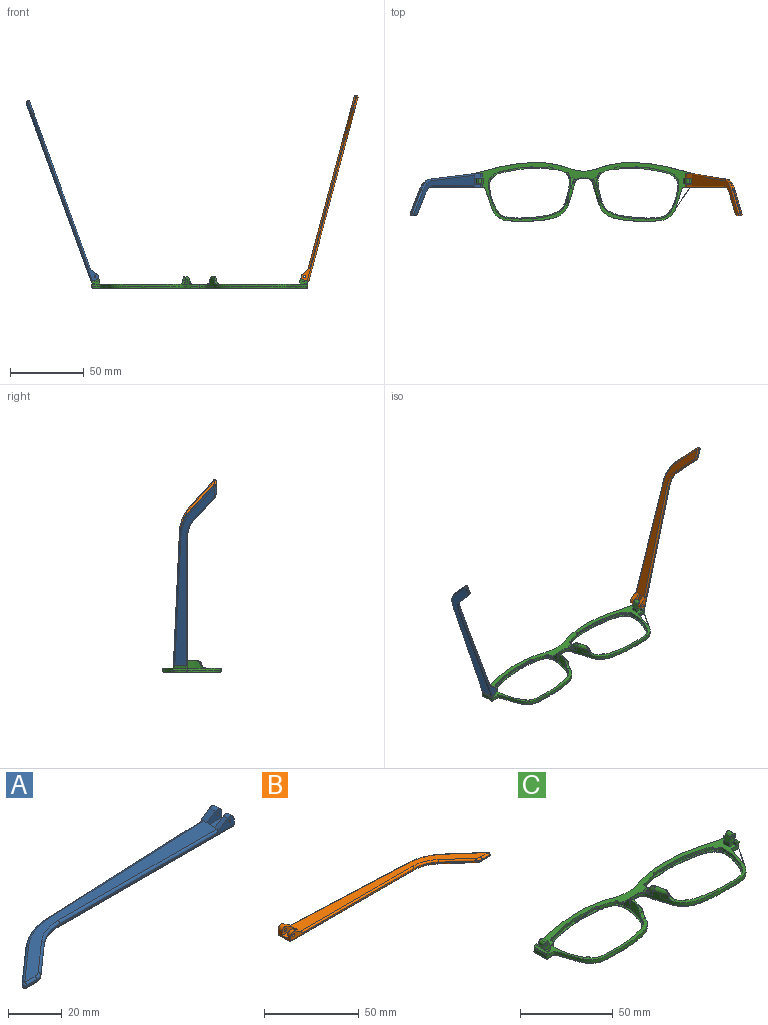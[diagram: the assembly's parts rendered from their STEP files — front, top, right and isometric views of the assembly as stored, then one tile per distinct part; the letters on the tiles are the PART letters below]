
ASSEMBLY  parts=3 mates=2
PART A: 43 faces, bbox 130.2x29.5x5.9 mm
  f0: plane 9.62x3.72mm, normal (1,0,0), area 24.7mm2, adj f1,f3,f4,f5,f10,f16,f18,f28
  f1: cylinder r=2.2mm len=3.45mm, axis (0,-1,0), area 11mm2, adj f0,f2,f4,f37
  f2: plane 6.01x3.91mm, normal (-0.55,0,0.84), area 12.7mm2, adj f1,f4,f9,f19,f37
  f3: plane 2.26x0.1mm, normal (0,0,1), area 0.1mm2, adj f0,f5,f18
  f4: plane 92.1x4.9mm, normal (0,-1,0), area 79.9mm2, adj f0,f1,f2,f14,f19,f36,f42
  f5: plane 93.42x4.13mm, normal (-0.04,1,0), area 64.8mm2, adj f0,f3,f11,f15,f17,f27,f28
  f6: plane 17.82x15.72mm, normal (-0.66,0.75,0), area 14.3mm2, adj f11,f12,f25,f30
  f7: plane 5.46x0.6mm, normal (0,-1,0), area 3.3mm2, adj f12,f13,f23,f32
  f8: plane 14.99x13.23mm, normal (0.66,-0.75,0), area 12mm2, adj f13,f14,f21,f34
  f9: plane 121.18x26.73mm, normal (0,0,1), area 627.7mm2, adj f2,f17,f19,f20,f21,f22,f23,f25
  f10: plane 129.1x27.08mm, normal (0,0,-1), area 686.5mm2, adj f0,f28,f29,f30,f32,f33,f34,f35
  f11: cylinder r=30mm len=18.52mm, axis (0,0,-1), area 12.2mm2, adj f5,f6,f26,f29
  f12: cylinder r=1mm len=1.75mm, axis (0,0,-1), area 1.5mm2, adj f6,f7,f24,f31
  f13: cylinder r=5mm len=3.31mm, axis (0,0,-1), area 2.2mm2, adj f7,f8,f22,f33
  f14: cylinder r=20mm len=13.23mm, axis (0,0,1), area 8.7mm2, adj f4,f8,f20,f35
  f15: plane 5.66x0.25mm, normal (0,0,-1), area 0.7mm2, adj f5,f17,f18
  f16: cylinder r=2.2mm len=3.45mm, axis (0,-1,0), area 14.8mm2, adj f0,f17,f18,f38
  f17: plane 6.01x3.91mm, normal (-0.55,0,0.84), area 16.9mm2, adj f5,f9,f15,f16,f18,f27,f38
  f18: plane 7.92x3.3mm, normal (0,1,0), area 15.9mm2, adj f0,f3,f15,f16,f17,f41
  f19: cylinder r=1mm len=84.18mm, axis (-1,0,0), area 131.4mm2, adj f2,f4,f9,f20
  f20: torus R=21mm, axis (0,0,1), area 23.1mm2, adj f9,f14,f19,f21
  f21: cylinder r=1mm len=15.65mm, axis (-0.75,-0.66,0), area 31.4mm2, adj f8,f9,f20,f22
  f22: torus R=4mm, axis (0,0,1), area 5.3mm2, adj f9,f13,f21,f23
  f23: cylinder r=1mm len=5.46mm, axis (-1,0,0), area 8.6mm2, adj f7,f9,f22,f24
  f24: sphere r=1mm, area 2.4mm2, adj f12,f23,f25
  f25: cylinder r=1mm len=18.48mm, axis (0.75,0.66,0), area 37.3mm2, adj f6,f9,f24,f26
  f26: torus R=29mm, axis (0,0,1), area 31.6mm2, adj f9,f11,f25,f27
  f27: cylinder r=1mm len=85.5mm, axis (1,0.04,0), area 133.5mm2, adj f5,f9,f17,f26
  f28: cylinder r=1mm len=93.46mm, axis (-1,-0.04,0), area 146.9mm2, adj f0,f5,f10,f29
  f29: torus R=29mm, axis (0,0,1), area 31.6mm2, adj f10,f11,f28,f30
  f30: cylinder r=1mm len=18.48mm, axis (-0.75,-0.66,0), area 37.3mm2, adj f6,f10,f29,f31
  f31: sphere r=1mm, area 2.4mm2, adj f12,f30,f32
  f32: cylinder r=1mm len=5.46mm, axis (1,0,0), area 8.6mm2, adj f7,f10,f31,f33
  f33: torus R=4mm, axis (0,0,1), area 5.3mm2, adj f10,f13,f32,f34
  f34: cylinder r=1mm len=15.65mm, axis (0.75,0.66,0), area 31.4mm2, adj f8,f10,f33,f35
  f35: torus R=21mm, axis (0,0,1), area 23.1mm2, adj f10,f14,f34,f36
  f36: cylinder r=1mm len=92.1mm, axis (1,0,0), area 144.7mm2, adj f0,f4,f10,f35
  f37: plane 7.92x4.7mm, normal (0,1,0), area 27mm2, adj f0,f1,f2,f39,f40,f42
  f38: plane 7.92x4.7mm, normal (0,-1,0), area 27mm2, adj f0,f16,f17,f39,f40,f41
  f39: plane 7.92x4.1mm, normal (0,0,1), area 32.5mm2, adj f0,f37,f38,f40
  f40: plane 4.1x1.4mm, normal (1,0,0), area 5.7mm2, adj f9,f37,f38,f39
  f41: cylinder r=0.5mm len=3.1mm, axis (0,-1,0), area 9.7mm2, adj f18,f38
  f42: cylinder r=0.5mm len=2.3mm, axis (0,-1,0), area 7.2mm2, adj f4,f37
PART B: 43 faces, bbox 130.2x29.5x5.9 mm
  f0: plane 9.62x3.72mm, normal (-1,0,0), area 24.7mm2, adj f1,f3,f4,f5,f10,f16,f18,f28
  f1: cylinder r=2.2mm len=3.45mm, axis (0,-1,0), area 11mm2, adj f0,f2,f4,f37
  f2: plane 6.01x3.91mm, normal (0.55,0,0.84), area 12.7mm2, adj f1,f4,f9,f19,f37
  f3: plane 2.26x0.1mm, normal (0,0,1), area 0.1mm2, adj f0,f5,f18
  f4: plane 92.1x4.9mm, normal (0,-1,0), area 78.2mm2, adj f0,f1,f2,f14,f19,f36,f42
  f5: plane 93.42x4.13mm, normal (0.04,1,0), area 64.8mm2, adj f0,f3,f11,f15,f17,f27,f28
  f6: plane 17.82x15.72mm, normal (0.66,0.75,0), area 14.3mm2, adj f11,f12,f25,f30
  f7: plane 5.46x0.6mm, normal (0,-1,0), area 3.3mm2, adj f12,f13,f23,f32
  f8: plane 14.99x13.23mm, normal (-0.66,-0.75,0), area 12mm2, adj f13,f14,f21,f34
  f9: plane 121.18x26.73mm, normal (0,0,1), area 627.7mm2, adj f2,f17,f19,f20,f21,f22,f23,f25
  f10: plane 129.1x27.08mm, normal (0,0,-1), area 686.5mm2, adj f0,f28,f29,f30,f32,f33,f34,f35
  f11: cylinder r=30mm len=18.52mm, axis (0,0,-1), area 12.2mm2, adj f5,f6,f26,f29
  f12: cylinder r=1mm len=1.75mm, axis (0,0,-1), area 1.5mm2, adj f6,f7,f24,f31
  f13: cylinder r=5mm len=3.31mm, axis (0,0,-1), area 2.2mm2, adj f7,f8,f22,f33
  f14: cylinder r=20mm len=13.23mm, axis (0,0,1), area 8.7mm2, adj f4,f8,f20,f35
  f15: plane 5.66x0.25mm, normal (0,0,-1), area 0.7mm2, adj f5,f17,f18
  f16: cylinder r=2.2mm len=3.45mm, axis (0,-1,0), area 14.8mm2, adj f0,f17,f18,f38
  f17: plane 6.01x3.91mm, normal (0.55,0,0.84), area 16.9mm2, adj f5,f9,f15,f16,f18,f27,f38
  f18: plane 7.92x3.3mm, normal (0,1,0), area 14.3mm2, adj f0,f3,f15,f16,f17,f41
  f19: cylinder r=1mm len=84.18mm, axis (1,0,0), area 131.4mm2, adj f2,f4,f9,f20
  f20: torus R=21mm, axis (0,0,1), area 23.1mm2, adj f9,f14,f19,f21
  f21: cylinder r=1mm len=15.65mm, axis (0.75,-0.66,0), area 31.4mm2, adj f8,f9,f20,f22
  f22: torus R=4mm, axis (0,0,1), area 5.3mm2, adj f9,f13,f21,f23
  f23: cylinder r=1mm len=5.46mm, axis (1,0,0), area 8.6mm2, adj f7,f9,f22,f24
  f24: sphere r=1mm, area 2.4mm2, adj f12,f23,f25
  f25: cylinder r=1mm len=18.48mm, axis (-0.75,0.66,0), area 37.3mm2, adj f6,f9,f24,f26
  f26: torus R=29mm, axis (0,0,1), area 31.6mm2, adj f9,f11,f25,f27
  f27: cylinder r=1mm len=85.5mm, axis (-1,0.04,0), area 133.5mm2, adj f5,f9,f17,f26
  f28: cylinder r=1mm len=93.46mm, axis (1,-0.04,0), area 146.9mm2, adj f0,f5,f10,f29
  f29: torus R=29mm, axis (0,0,1), area 31.6mm2, adj f10,f11,f28,f30
  f30: cylinder r=1mm len=18.48mm, axis (0.75,-0.66,0), area 37.3mm2, adj f6,f10,f29,f31
  f31: sphere r=1mm, area 2.4mm2, adj f12,f30,f32
  f32: cylinder r=1mm len=5.46mm, axis (-1,0,0), area 8.6mm2, adj f7,f10,f31,f33
  f33: torus R=4mm, axis (0,0,1), area 5.3mm2, adj f10,f13,f32,f34
  f34: cylinder r=1mm len=15.65mm, axis (-0.75,0.66,0), area 31.4mm2, adj f8,f10,f33,f35
  f35: torus R=21mm, axis (0,0,1), area 23.1mm2, adj f10,f14,f34,f36
  f36: cylinder r=1mm len=92.1mm, axis (-1,0,0), area 144.7mm2, adj f0,f4,f10,f35
  f37: plane 7.92x4.7mm, normal (0,1,0), area 25.4mm2, adj f0,f1,f2,f39,f40,f42
  f38: plane 7.92x4.7mm, normal (0,-1,0), area 25.4mm2, adj f0,f16,f17,f39,f40,f41
  f39: plane 7.92x4.1mm, normal (0,0,1), area 32.5mm2, adj f0,f37,f38,f40
  f40: plane 4.1x1.4mm, normal (-1,0,0), area 5.7mm2, adj f9,f37,f38,f39
  f41: cylinder r=0.88mm len=3.1mm, axis (0,-1,0), area 17mm2, adj f18,f38
  f42: cylinder r=0.88mm len=2.3mm, axis (0,-1,0), area 12.6mm2, adj f4,f37
PART C: 120 faces, bbox 148.1x40.9x10.4 mm
  f0: bspline ~1.82x1.22mm, area 0.7mm2, adj f1,f116,f118,f119
  f1: bspline ~2.66x2.04mm, area 1.9mm2, adj f0,f2,f115,f116,f119
  f2: bspline ~3.55x3.47mm, area 3.7mm2, adj f1,f3,f114,f115,f119
  f3: plane 147.7x40.47mm, normal (0,0,1), area 882.9mm2, adj f2,f4,f16,f17,f18,f19,f20,f21
  f4: plane 1.23x0.04mm, normal (0,0,1), area 0mm2, adj f3,f5,f116
  f5: plane 2.76x2.53mm, normal (0,-1,0), area 3.9mm2, adj f4,f6,f15,f16,f24
  f6: plane 9.65x1.24mm, normal (0,0,1), area 8.2mm2, adj f5,f7,f14,f15,f19,f20,f21,f24
  f7: plane 5.77x5.06mm, normal (0,-1,0), area 17mm2, adj f6,f8,f9,f11,f12,f13,f14,f23
  f8: cylinder r=1.98mm len=4mm, axis (0,-1,0), area 12.4mm2, adj f7,f12,f14,f21
  f9: plane 4x3.31mm, normal (-0.94,0,0.34), area 14.1mm2, adj f7,f10,f11,f21
  f10: plane 4x0.02mm, normal (0.34,0,0.94), area 0.1mm2, adj f9,f21,f22
  f11: cylinder r=1.98mm len=4mm, axis (0,1,0), area 12.4mm2, adj f7,f9,f12,f21
  f12: plane 4x0.01mm, normal (0.34,0,0.94), area 0mm2, adj f7,f8,f11,f21
  f13: cylinder r=0.88mm len=4mm, axis (0,-1,0), area 22mm2, adj f7,f21
  f14: plane 4x2.21mm, normal (0.94,0,-0.34), area 9.4mm2, adj f6,f7,f8,f21
  f15: plane 9.71x1.44mm, normal (0.34,0,0.94), area 13.9mm2, adj f5,f6,f16,f17,f18,f19
  f16: cone r=1mm half-angle=20deg, axis (0,0,1), area 2.3mm2, adj f3,f5,f15,f17
  f17: plane 7.67x1.6mm, normal (0.94,0,-0.34), area 13mm2, adj f3,f15,f16,f18
  f18: cylinder r=1mm len=2.28mm, axis (-0.34,0,-0.94), area 3mm2, adj f3,f15,f17,f19
  f19: plane 2.1x1.69mm, normal (0,1,0), area 2.8mm2, adj f3,f6,f15,f18,f20
  f20: plane 3.3x2.1mm, normal (-1,0,0), area 6.9mm2, adj f3,f6,f19,f21
  f21: plane 6.97x5.07mm, normal (0,1,0), area 22.7mm2, adj f3,f6,f8,f9,f10,f11,f12,f13
  f22: plane 4x2.36mm, normal (-1,0,0), area 9.5mm2, adj f3,f10,f21,f23
  f23: plane 3.2x2.36mm, normal (0,-1,0), area 5.7mm2, adj f3,f7,f22,f24
  f24: plane 2.35x2.1mm, normal (-1,0,0), area 4.9mm2, adj f3,f5,f6,f7,f23
  f25: bspline ~3.69x3.66mm, area 7.8mm2, adj f3,f26,f31,f59,f116
  f26: bspline ~7.26x7.26mm, area 6.3mm2, adj f25,f27,f31,f59
  f27: bspline ~10.3x4.84mm, area 21.4mm2, adj f26,f28,f31,f59,f116,f119
  f28: plane 3.63x0.97mm, normal (0,0,1), area 0.3mm2, adj f27,f29,f59
  f29: bspline ~8.14x4.16mm, area 6.6mm2, adj f28,f30,f59,f114,f119
  f30: extruded ~4.98x1.44mm, area 6.9mm2, adj f29,f59
  f31: extruded ~4.44x3.32mm, area 15.1mm2, adj f25,f26,f27,f32,f116
  f32: plane 4.46x1.45mm, normal (0,0,1), area 0.1mm2, adj f31,f116
  f33: cylinder r=1.3mm len=1.78mm, axis (0,0,1), area 1.3mm2, adj f3,f34,f59
  f34: plane 1.79x1.31mm, normal (0,0,-1), area 0.9mm2, adj f33,f59
  f35: cylinder r=1.3mm len=1.93mm, axis (0,0,1), area 1.5mm2, adj f3,f36,f59
  f36: plane 1.95x1.68mm, normal (0,0,-1), area 1.5mm2, adj f35,f59
  f37: cylinder r=2.28mm len=3.13mm, axis (0,0,1), area 2.5mm2, adj f3,f38,f59
  f38: plane 3.14x2.79mm, normal (0,0,-1), area 3.9mm2, adj f37,f59
  f39: extruded ~8.63x2.7mm, area 18.4mm2, adj f3,f40,f58,f59
  f40: bspline ~56.23x35.9mm, area 235.3mm2, adj f39,f41,f42
  f41: plane 56.09x35.62mm, normal (0,0,1), area 124.3mm2, adj f40,f58
  f42: plane 144.78x37.85mm, normal (0,0,-1), area 582.4mm2, adj f40,f43,f46,f49,f50,f51,f52,f54
  f43: bspline ~56.22x35.9mm, area 235.3mm2, adj f42,f44,f81
  f44: plane 56.09x35.62mm, normal (0,0,1), area 124.3mm2, adj f43,f45
  f45: extruded ~55.59x35.37mm, area 140.2mm2, adj f44,f81,f88
  f46: bspline ~8.99x1.23mm, area 12.6mm2, adj f42,f47,f48,f116
  f47: bspline ~1x1mm, area 0.8mm2, adj f46,f57,f116
  f48: bspline ~1.04x1mm, area 0.7mm2, adj f46,f49,f116
  f49: bspline ~45.86x8.59mm, area 59.8mm2, adj f42,f48,f50,f116
  f50: bspline ~37.01x6.7mm, area 56.6mm2, adj f42,f49,f51,f113
  f51: bspline ~37.01x6.7mm, area 56.6mm2, adj f42,f50,f52,f112
  f52: bspline ~45.86x8.59mm, area 59.8mm2, adj f42,f51,f53,f111
  f53: bspline ~1.04x1mm, area 0.8mm2, adj f52,f54,f111
  f54: bspline ~8.99x1.23mm, area 12.6mm2, adj f42,f53,f55,f111
  f55: bspline ~1x1mm, area 0.8mm2, adj f54,f56,f111
  f56: bspline ~73.83x30.39mm, area 161.7mm2, adj f42,f55,f57,f111
  f57: bspline ~73.27x30.39mm, area 161.7mm2, adj f42,f47,f56,f116
  f58: extruded ~55.59x35.37mm, area 140.2mm2, adj f39,f41,f59
  f59: extruded ~55.59x35.37mm, area 208.7mm2, adj f3,f25,f26,f27,f28,f29,f30,f33
  f60: plane 3.25x1.39mm, normal (0,0,-1), area 2.1mm2, adj f59,f61
  f61: cylinder r=2.28mm len=3.21mm, axis (0,0,1), area 2.2mm2, adj f3,f59,f60,f114
  f62: bspline ~6.38x2.14mm, area 2.6mm2, adj f3,f63,f115,f116
  f63: bspline ~6.38x2.14mm, area 2.6mm2, adj f3,f62,f64,f111
  f64: bspline ~2.1x1.46mm, area 0.6mm2, adj f63,f65,f77,f111
  f65: bspline ~2.66x2.03mm, area 1.9mm2, adj f64,f66,f69,f77,f111
  f66: bspline ~2.19x1.4mm, area 0.7mm2, adj f65,f67,f69,f111
  f67: extruded ~3.67x3.11mm, area 5.9mm2, adj f66,f68,f69,f111
  f68: bspline ~5.24x1.75mm, area 0mm2, adj f67,f111
  f69: bspline ~6.09x4.93mm, area 12.6mm2, adj f65,f66,f67,f70,f75,f77,f111
  f70: bspline ~10.3x4.84mm, area 21.5mm2, adj f69,f71,f72,f74,f88,f111
  f71: plane 3.63x0.97mm, normal (0,0,1), area 0.3mm2, adj f70,f75,f88
  f72: extruded ~4.44x3.32mm, area 15.1mm2, adj f70,f73,f74,f89,f111
  f73: plane 4.46x1.45mm, normal (0,0,1), area 0.1mm2, adj f72,f111
  f74: bspline ~7.26x7.26mm, area 6.2mm2, adj f70,f72,f88,f89
  f75: bspline ~8.14x4.16mm, area 6.4mm2, adj f69,f71,f76,f78,f88
  f76: extruded ~4.98x1.44mm, area 6.9mm2, adj f75,f88
  f77: bspline ~3.55x3.47mm, area 3.7mm2, adj f3,f64,f65,f69,f78
  f78: bspline ~4.88x3.94mm, area 7.9mm2, adj f3,f75,f77,f79,f88
  f79: cylinder r=2.28mm len=3.21mm, axis (0,0,1), area 2.2mm2, adj f3,f78,f80,f88
  f80: plane 3.25x1.39mm, normal (0,0,-1), area 2.1mm2, adj f79,f88
  f81: extruded ~8.63x2.7mm, area 18.4mm2, adj f3,f43,f45,f88
  f82: cylinder r=2.28mm len=3.13mm, axis (0,0,1), area 2.5mm2, adj f3,f83,f88
  f83: plane 3.14x2.79mm, normal (0,0,-1), area 3.9mm2, adj f82,f88
  f84: cylinder r=1.3mm len=1.93mm, axis (0,0,1), area 1.5mm2, adj f3,f85,f88
  f85: plane 1.95x1.68mm, normal (0,0,-1), area 1.5mm2, adj f84,f88
  f86: cylinder r=1.3mm len=1.78mm, axis (0,0,1), area 1.3mm2, adj f3,f87,f88
  f87: plane 1.79x1.31mm, normal (0,0,-1), area 0.9mm2, adj f86,f88
  f88: extruded ~55.59x35.37mm, area 208.9mm2, adj f3,f45,f70,f71,f74,f75,f76,f78
  f89: bspline ~3.69x3.66mm, area 7.8mm2, adj f3,f72,f74,f88,f111
  f90: plane 2.35x2.1mm, normal (1,0,0), area 4.9mm2, adj f3,f91,f93,f100,f102
  f91: plane 2.76x2.53mm, normal (0,-1,0), area 3.9mm2, adj f90,f92,f93,f109,f110
  f92: plane 9.71x1.44mm, normal (-0.34,0,0.94), area 13.9mm2, adj f91,f93,f106,f107,f108,f109
  f93: plane 9.65x1.24mm, normal (0,0,1), area 8.2mm2, adj f90,f91,f92,f94,f100,f104,f105,f106
  f94: plane 4x2.21mm, normal (-0.94,0,-0.34), area 9.4mm2, adj f93,f95,f100,f104
  f95: cylinder r=1.98mm len=4mm, axis (0,-1,0), area 12.4mm2, adj f94,f96,f100,f104
  f96: plane 4x0.01mm, normal (-0.34,0,0.94), area 0mm2, adj f95,f97,f100,f104
  f97: cylinder r=1.98mm len=4mm, axis (0,1,0), area 12.4mm2, adj f96,f98,f100,f104
  f98: plane 4x3.31mm, normal (0.94,0,0.34), area 14.1mm2, adj f97,f99,f100,f104
  f99: plane 4x0.02mm, normal (-0.34,0,0.94), area 0.1mm2, adj f98,f103,f104
  f100: plane 5.77x5.06mm, normal (0,-1,0), area 17mm2, adj f90,f93,f94,f95,f96,f97,f98,f101
  f101: cylinder r=0.88mm len=4mm, axis (0,-1,0), area 22mm2, adj f100,f104
  f102: plane 3.2x2.36mm, normal (0,-1,0), area 5.7mm2, adj f3,f90,f100,f103
  f103: plane 4x2.36mm, normal (1,0,0), area 9.5mm2, adj f3,f99,f102,f104
  f104: plane 6.97x5.07mm, normal (0,1,0), area 22.7mm2, adj f3,f93,f94,f95,f96,f97,f98,f99
  f105: plane 3.3x2.1mm, normal (1,0,0), area 6.9mm2, adj f3,f93,f104,f106
  f106: plane 2.1x1.69mm, normal (0,1,0), area 2.8mm2, adj f3,f92,f93,f105,f107
  f107: cylinder r=1mm len=2.28mm, axis (0.34,0,-0.94), area 3mm2, adj f3,f92,f106,f108
  f108: plane 7.67x1.6mm, normal (-0.94,0,-0.34), area 13mm2, adj f3,f92,f107,f109
  f109: cone r=1mm half-angle=20deg, axis (0,0,1), area 2.3mm2, adj f3,f91,f92,f108
  f110: plane 1.23x0.04mm, normal (0,0,1), area 0mm2, adj f3,f91,f111
  f111: extruded ~73.26x39.84mm, area 292.7mm2, adj f3,f52,f53,f54,f55,f56,f63,f64
  f112: extruded ~35.39x5.69mm, area 72.2mm2, adj f3,f51,f111,f113
  f113: extruded ~35.39x5.69mm, area 72.2mm2, adj f3,f50,f112,f116
  f114: bspline ~6.16x4.45mm, area 7.9mm2, adj f2,f3,f29,f59,f61
  f115: bspline ~1.82x1.13mm, area 0.6mm2, adj f1,f2,f62,f116
  f116: extruded ~73.26x39.84mm, area 292.7mm2, adj f0,f1,f3,f4,f25,f27,f31,f32
  f117: bspline ~5.24x1.75mm, area 0mm2, adj f116,f118
  f118: extruded ~3.67x3.11mm, area 5.9mm2, adj f0,f116,f117,f119
  f119: bspline ~6.09x4.93mm, area 12.7mm2, adj f0,f1,f2,f27,f29,f116,f118
PLACE A rot(axis=(0,1,0),70deg) t=(-84.77,-5.75,56)mm
PLACE B rot(axis=(0,-1,0),75deg) t=(68.2,-5.75,-61.61)mm
PLACE C t=(10.15,-1.13,-5.77)mm
MATE revolute A.f1 <-> C.f97  axis (0,-1,0) through (-60.89,2.72,1.22)mm
MATE revolute B.f41 <-> C.f8  axis (0,-1,0) through (81.2,2.72,1.21)mm
